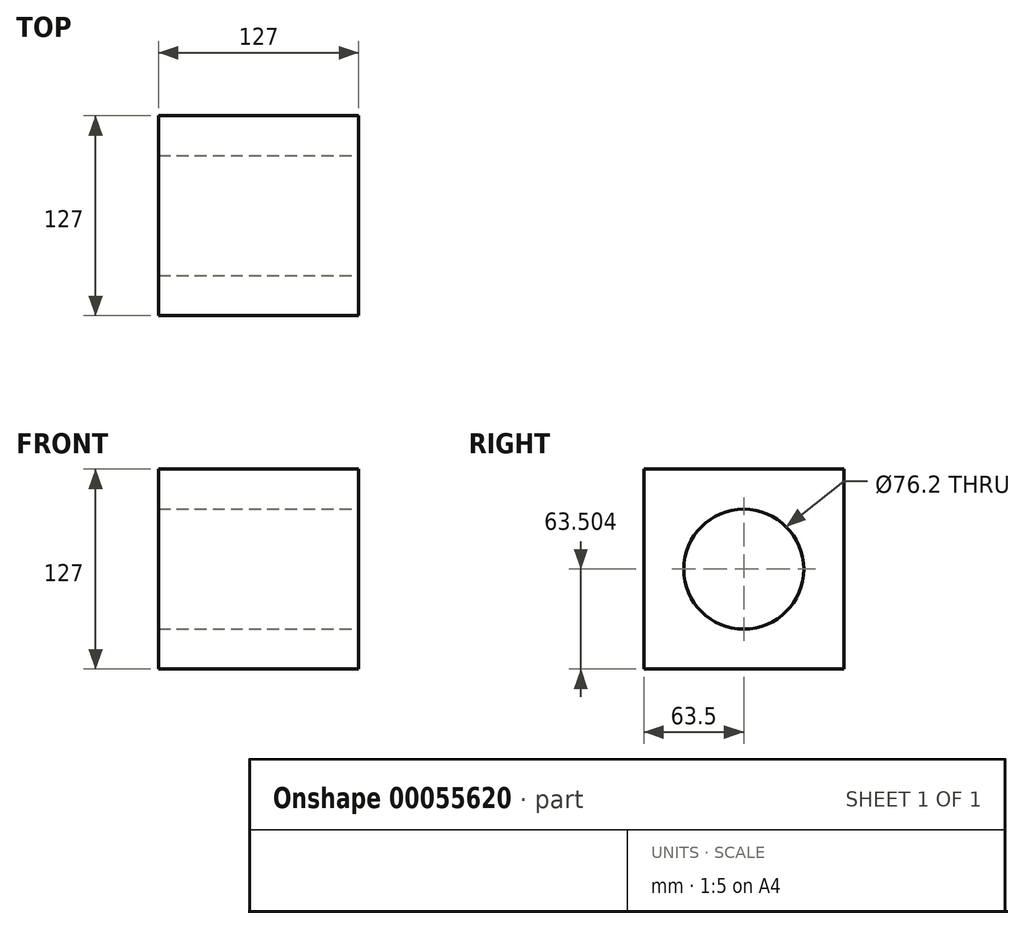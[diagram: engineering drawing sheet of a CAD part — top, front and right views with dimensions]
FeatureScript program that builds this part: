
annotation { "Feature Type Name" : "Feature", "Feature Type Description" : "" }
export const myFeature = defineFeature(function(context is Context, id is Id, definition is map)
    precondition{}
    {
        {
            var Q0;
            Q0=qCreatedBy(makeId("Front.planeOp"),FACE);
            var sketch = newSketch(context, id + "F0", { "sketchPlane" : qUnion([Q0])});
            skLineSegment(sketch, "E0.bottom", {"start": v(-63.95, 62.11) * mm, "end": v(63.05, 62.11) * mm});
            skLineSegment(sketch, "E0.top", {"start": v(-63.95, -64.89) * mm, "end": v(63.05, -64.89) * mm});
            skLineSegment(sketch, "E0.left", {"start": v(-63.95, 62.11) * mm, "end": v(-63.95, -64.89) * mm});
            skLineSegment(sketch, "E0.right", {"start": v(63.05, 62.11) * mm, "end": v(63.05, -64.89) * mm});
            skSolve(sketch);
        }
        {
            var Q0;
            Q0=makeQuery(id+"F0.imprint","IMPRINT",FACE,{"disambiguationData":[TD([[makeQuery(id+"F0.imprint","IMPRINT",EDGE,{"derivedFrom":sQuery(id+"F0.wireOp",EDGE,"E0.bottom")}),-1.0]])]});
            extrude(context, id + "F1", {"entities" : qUnion([Q0]), "depth" : 127 * mm});
        }
        {
            var Q0;
            Q0=makeQuery(id+"F1.opExtrude","SWEPT_FACE",FACE,{"disambiguationData":[OSD([sQuery(id+"F0.wireOp",EDGE,"E0.right")])]});
            var sketch = newSketch(context, id + "F2", { "sketchPlane" : qUnion([Q0])});
            skCircle(sketch, "E1", {"center": v(-63.5, -1.39) * mm, "radius": 38.1 * mm});
            skSolve(sketch);
        }
        {
            var Q0;
            Q0=makeQuery(id+"F2.imprint","IMPRINT",FACE,{"disambiguationData":[TD([[makeQuery(id+"F2.imprint","IMPRINT",EDGE,{"derivedFrom":sQuery(id+"F2.wireOp",EDGE,"E1")}),1.0]])]});
            extrude(context, id + "F3", {"entities" : qUnion([Q0]), "operationType" : NewBodyOperationType.REMOVE, "oppositeDirection" : true, "depth" : 127 * mm});
        }
    });
